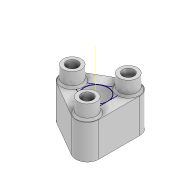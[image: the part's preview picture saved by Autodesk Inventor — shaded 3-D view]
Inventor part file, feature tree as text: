
AUTODESK INVENTOR PART (.ipt)
format: ipt  version: 2020 (Build 240168000, 168)  size: 163,328 bytes
history: native  units: mm
features: sketch x5, extrude x4, pattern_circular x2, other x1, thicken_offset x1, fillet x1, chamfer x1
ambient origin geometry x8: Origin, YZ Plane, XZ Plane, XY Plane, X Axis, Y Axis, Z Axis, Center Point
bodies: Solid1 (feature_tree)
feature tree (15):
  extrude  "Extrusion1"  TaperAngle=30.0deg  [1 undecoded]
  extrude  "Extrusion2"  TaperAngle=60.0deg  [1 undecoded]
  sketch  "Sketch8"  dims[d4=9.0mm d5=0.0mm]
  other  "Work Axis3"
  pattern_circular  "Circular Pattern3"  Count=3 Angle=360.0deg
  thicken_offset  "Thicken2"
  fillet  "Fillet2"  Radius=3.0mm
  chamfer  "Chamfer3"  Distance=3.0mm
  extrude  "Extrusion5"  Depth=3.0mm TaperAngle=45.0deg
  extrude  "Extrusion6"  Depth=3.0mm
  pattern_circular  "Circular Pattern4"  [2 undecoded]
  sketch  "Sketch1"  dims[d0=10.73mm d1=30.0deg]
  sketch  "Sketch2"  dims[d2=10.73mm d3=60.0deg]
  sketch  "Sketch11"  dims[d6=4.7625mm]
  sketch  "Sketch12"  dims[d7=3.7mm d8=0.0mm d30=30.0mm d31=360.0deg d33=3.0mm d34=5.0mm d35=3.0mm d36=0.5mm d37=2.0mm d38=45.0deg d39=6.45mm d40=10.0mm d41=0.0mm d42=3.0mm d43=20.0mm d44=0.0mm d45=30.0mm d46=360.0deg]
note: 4 required parameter values undecoded (feature->parameter linkage not recoverable at this tier; creation-order binding heuristic only, values carry confidence <= 0.55)
